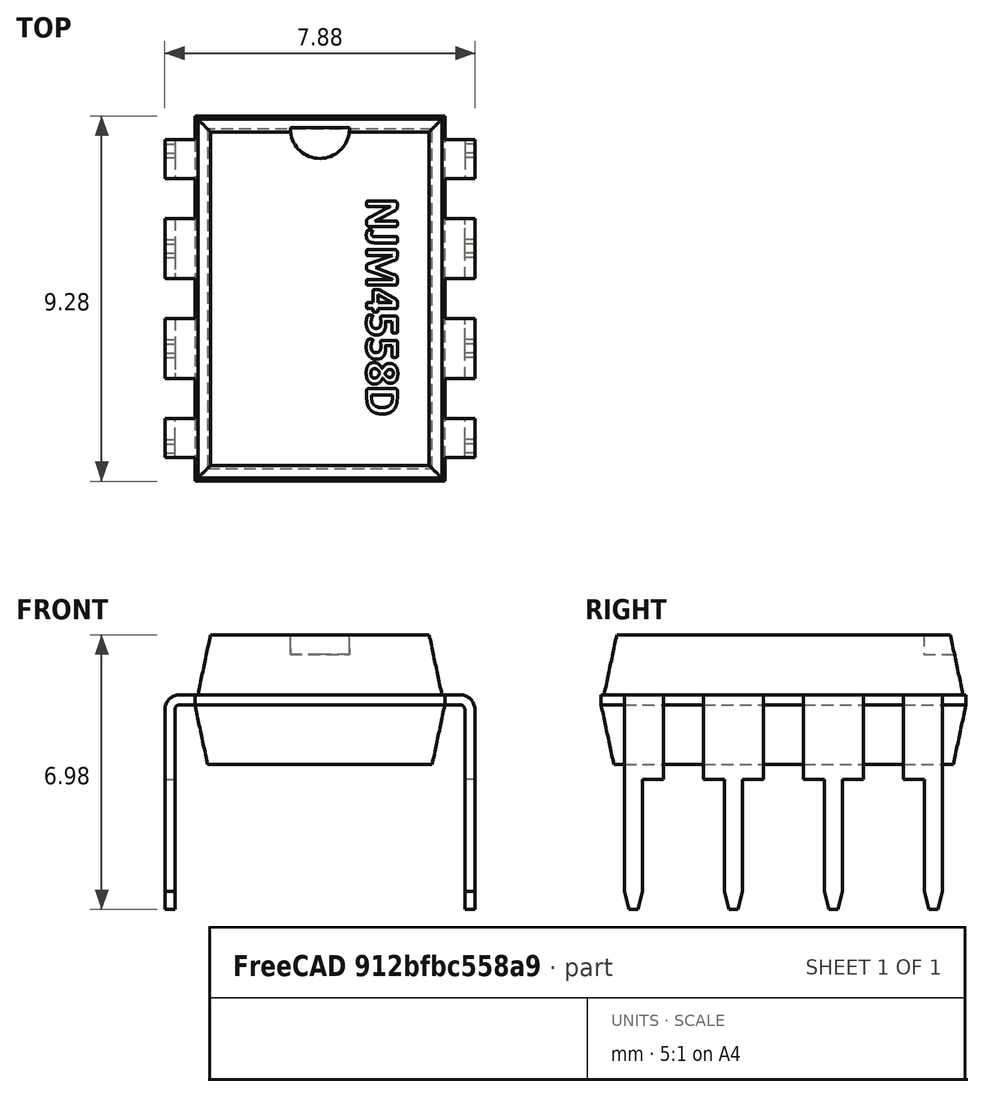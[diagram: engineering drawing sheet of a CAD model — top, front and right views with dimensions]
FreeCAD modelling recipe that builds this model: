
FCSTD DOCUMENT  (FreeCAD 0.17R13528 (Git))
Label: NicerTemplate
License: All rights reserved
LicenseURL: http://en.wikipedia.org/wiki/All_rights_reserved
objects: Part::Feature×1, Part::Part2DObjectPython×1, Part::Extrusion×1, Part::Cut×1
note: 4 computed .brp shape members not serialized (recipe doc carries the construction recipe); baked Part::Feature solids carry a one-line shape summary decoded from their .brp

FEATURE [Part::Feature] Part__Feature  label="DIP-8_W7.62mm"
  shape: bbox 7.874 x 9.27 x 6.98 mm, 148 faces (baked)
FEATURE [Part::Part2DObjectPython] ShapeString  # Draft 2D object (typed FeaturePython)
  FontFile = <userpath>/Desktop/Freecad Projects/calibrib.ttf
  Placement = pos=(5,-1.25,3.7) rot=(0,0,1;-1.5708rad)
  Size = 1
  String = NJM4558D
  Support = -> [Part__Feature]
  Tracking = 0
FEATURE [Part::Extrusion] Extrude
  Base = -> ShapeString
  Dir = (0,0,1)
  DirMode = 2
  FaceMakerClass = Part::FaceMakerBullseye
  LengthFwd = -0.025
  LengthRev = 0
  Solid = true
  Symmetric = false
FEATURE [Part::Cut] Cut
  Base = -> Part__Feature
  Tool = -> Extrude
